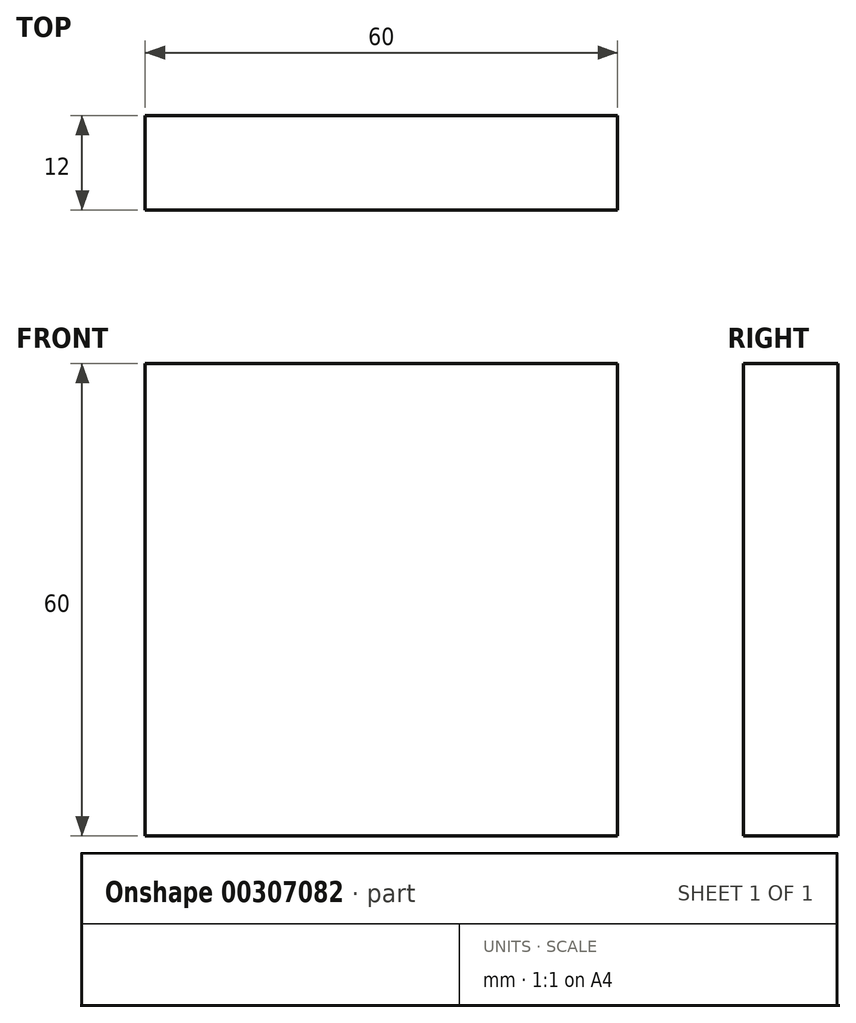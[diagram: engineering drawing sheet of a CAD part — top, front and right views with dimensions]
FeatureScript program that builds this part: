
annotation { "Feature Type Name" : "Feature", "Feature Type Description" : "" }
export const myFeature = defineFeature(function(context is Context, id is Id, definition is map)
    precondition{}
    {
        {
            var Q0;
            Q0=qCreatedBy(makeId("Front.planeOp"),FACE);
            var sketch = newSketch(context, id + "F0", { "sketchPlane" : qUnion([Q0])});
            skLineSegment(sketch, "E0.bottom", {"start": v(-27.97, 29.62) * mm, "end": v(32.03, 29.62) * mm});
            skLineSegment(sketch, "E0.top", {"start": v(-27.97, -30.38) * mm, "end": v(32.03, -30.38) * mm});
            skLineSegment(sketch, "E0.left", {"start": v(-27.97, 29.62) * mm, "end": v(-27.97, -30.38) * mm});
            skLineSegment(sketch, "E0.right", {"start": v(32.03, 29.62) * mm, "end": v(32.03, -30.38) * mm});
            skSolve(sketch);
        }
        {
            var Q0;
            Q0=makeQuery(id+"F0.imprint","IMPRINT",FACE,{"disambiguationData":[TD([[makeQuery(id+"F0.imprint","IMPRINT",EDGE,{"derivedFrom":sQuery(id+"F0.wireOp",EDGE,"E0.bottom")}),-1.0]])]});
            extrude(context, id + "F1", {"entities" : qUnion([Q0]), "depth" : 12 * mm});
        }
    });
